# Revit family: JC KONTAKTER JCK119 FI
name_source: partatom
category: Specialty Equipment
units: mm (PartAtom-declared; Revit-internal decimal feet)

## family parameters
Cut with Voids When Loaded = No
Enable Cutting in Views = Yes
Host = Face
Maintain Annotation Orientation = Yes
Part Type = Normal
Room Calculation Point = No
Round Connector Dimension = Use Diameter
Shared = No

## types (1)
- JCK119
    CE asiakirja = https://jckontakter.se
    Default Elevation = 800 mm  [stored 2.62467 ft]
    Description = Kyynärkytkin JCK119 on vankkarakenteinen malli, jossa on litteä painolevy ja messinkinen päätykappale sekä kullanväriseksi anodisoidusta alumiinista valmistettu runko-osa. Tämä malli on suunniteltu käytettäväksi ylellisissä ympäristöissä ja suojelluissa rakennuksissa. Kyynärkytkin JCK119 voidaan tilata myös langattomalla ohjauksella, sillä vanhoissa rakennuksissa kaapelointiin liittyy usein haasteita.
    Kansi = Messinki
    Kotelo = Aluminum ENAW 6060 (kulta-anodisoitu)
    Manufacturer = JC Kontakter
    Mikrokytkimien määrä = 2
    Mikrokytkin = Standar NO IP67
    Model = JCK119
    Nimellisestä nimellisvirrasta = 1mA/4 V DC
    Pienin nimellisvirta = 12V Resistiivinen 6A Induktiivinen L/R 5ms 6A, 24V Resistiivinen 6A Induktiivinen L/R 5ms 5A
    Päätypäät = Messinki
    Tekniken tuotekortti = https://www.jckontakter.fi
    Tuotteen paino = 0.619 kg
    URL = https://www.jckontakter.fi
    Valmistusmaa = Ruotsi

note: [stored X ft] marks values corroborated as IEEE doubles in the binary element streams (Revit-internal decimal feet)

## geometry (parser evidence)
native form markers: Sweep x6
no freeform markers — native parametric forms only
